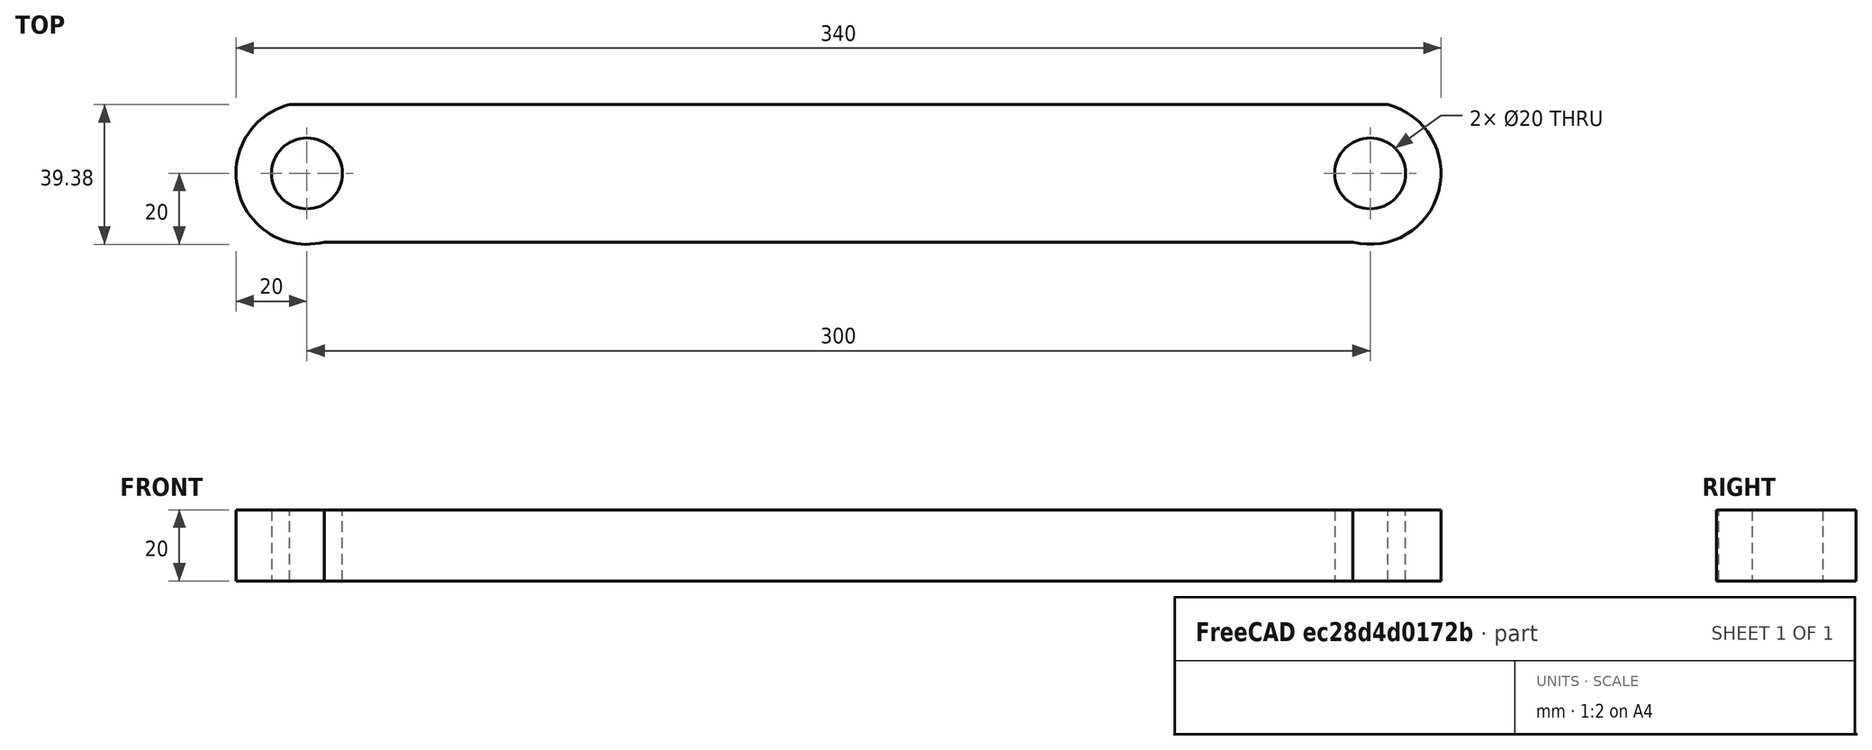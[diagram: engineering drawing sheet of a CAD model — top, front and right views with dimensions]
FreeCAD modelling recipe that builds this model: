
FCSTD DOCUMENT  (FreeCAD 0.20R29177 +426 (Git))
Label: brackets
License: All rights reserved
LicenseURL: http://en.wikipedia.org/wiki/All_rights_reserved
objects: Sketcher::SketchObject×1, PartDesign::Body×1, Part::Extrusion×1
note: 3 computed .brp shape members not serialized (recipe doc carries the construction recipe); baked Part::Feature solids carry a one-line shape summary decoded from their .brp

FEATURE [Sketcher::SketchObject] Sketch
  FullyConstrained = false
  MapMode = 5
  Support = -> [XY_Plane]
  sketch-geometry (7):
    g0: ArcOfCircle CenterX=0 CenterY=0 CenterZ=0 NormalX=0 NormalY=0 NormalZ=1 AngleXU=0 Radius=20 StartAngle=1.82032 EndAngle=4.96191
    g1: Circle CenterX=0 CenterY=0 CenterZ=0 NormalX=0 NormalY=0 NormalZ=1 AngleXU=0 Radius=10
    g2: LineSegment StartX=0 StartY=0 StartZ=0 EndX=300 EndY=0 EndZ=0
    g3: Circle CenterX=300 CenterY=0 CenterZ=0 NormalX=0 NormalY=0 NormalZ=1 AngleXU=0 Radius=10
    g4: ArcOfCircle CenterX=300 CenterY=0 CenterZ=0 NormalX=0 NormalY=0 NormalZ=1 AngleXU=0 Radius=20 StartAngle=4.46286 EndAngle=7.60446
    g5: LineSegment StartX=-4.93888 StartY=19.3806 StartZ=0 EndX=304.939 EndY=19.3806 EndZ=0
    g6: LineSegment StartX=4.93888 StartY=-19.3806 StartZ=0 EndX=295.061 EndY=-19.3806 EndZ=0
  constraints (18):
    c: Coincident(g0,g-1)
    c: Coincident(g1,g0)
    c: Coincident(g2,g0)
    c: PointOnObject(g2,g-1)
    c: Coincident(g3,g2)
    c: Coincident(g4,g2)
    c: Equal(g4,g0)
    c: Equal(g3,g1)
    c: DistanceX(g0,g3) = 300
    c: Horizontal(g5)
    c: Horizontal(g6)
    c: Coincident(g0,g5)
    c: Coincident(g0,g6)
    c: Coincident(g4,g5)
    c: Coincident(g4,g6)
    c: Symmetric(g4,g4,g3)
    c: Diameter(g1) = 20
    c: Diameter(g0) = 40
FEATURE [PartDesign::Body] Body
  Group = -> [Sketch]
  Origin = -> Origin
FEATURE [Part::Extrusion] Extrude
  Base = -> Sketch
  Dir = (0,0,1)
  DirMode = 2
  FaceMakerClass = Part::FaceMakerBullseye
  LengthFwd = 20
  LengthRev = 0
  Solid = true
  Symmetric = false
